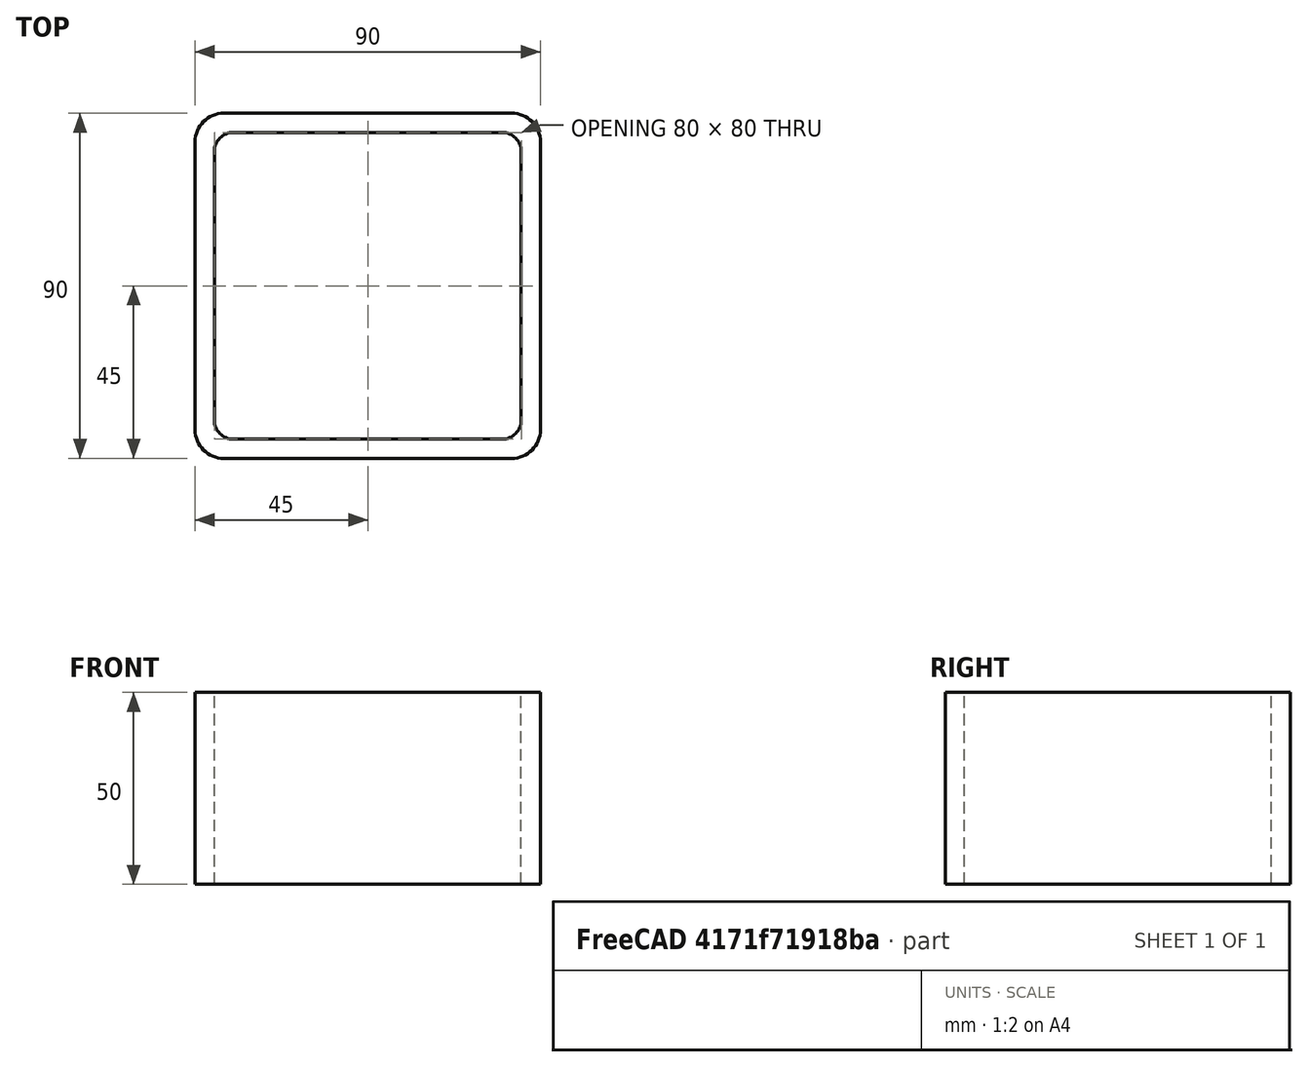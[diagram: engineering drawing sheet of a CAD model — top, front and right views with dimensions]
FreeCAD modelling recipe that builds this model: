
FCSTD DOCUMENT  (FreeCAD 0.15R4671 (Git))
Label: Square hollow section 90x90x5 EN10219 S235JRH
License: All rights reserved
LicenseURL: http://en.wikipedia.org/wiki/All_rights_reserved
objects: Sketcher::SketchObject×1, Part::Extrusion×1
note: 2 computed .brp shape members not serialized (recipe doc carries the construction recipe); baked Part::Feature solids carry a one-line shape summary decoded from their .brp

FEATURE [Sketcher::SketchObject] Sketch
  sketch-geometry (16):
    g0: LineSegment StartX=-35 StartY=40 StartZ=0 EndX=35 EndY=40 EndZ=0
    g1: LineSegment StartX=40 StartY=35 StartZ=0 EndX=40 EndY=-35 EndZ=0
    g2: LineSegment StartX=35 StartY=-40 StartZ=0 EndX=-35 EndY=-40 EndZ=0
    g3: LineSegment StartX=-40 StartY=-35 StartZ=0 EndX=-40 EndY=35 EndZ=0
    g4: LineSegment StartX=-37.5 StartY=45 StartZ=0 EndX=37.5 EndY=45 EndZ=0
    g5: LineSegment StartX=45 StartY=37.5 StartZ=0 EndX=45 EndY=-37.5 EndZ=0
    g6: LineSegment StartX=37.5 StartY=-45 StartZ=0 EndX=-37.5 EndY=-45 EndZ=0
    g7: LineSegment StartX=-45 StartY=-37.5 StartZ=0 EndX=-45 EndY=37.5 EndZ=0
    g8: ArcOfCircle CenterX=-35 CenterY=35 CenterZ=0 NormalX=0 NormalY=0 NormalZ=1 Radius=5 StartAngle=1.5708 EndAngle=3.14159
    g9: ArcOfCircle CenterX=35 CenterY=35 CenterZ=0 NormalX=0 NormalY=0 NormalZ=1 Radius=5 StartAngle=0 EndAngle=1.5708
    g10: ArcOfCircle CenterX=35 CenterY=-35 CenterZ=0 NormalX=0 NormalY=0 NormalZ=1 Radius=5 StartAngle=4.71239 EndAngle=6.28319
    g11: ArcOfCircle CenterX=-35 CenterY=-35 CenterZ=0 NormalX=0 NormalY=0 NormalZ=1 Radius=5 StartAngle=3.14159 EndAngle=4.71239
    g12: ArcOfCircle CenterX=37.5 CenterY=37.5 CenterZ=0 NormalX=0 NormalY=0 NormalZ=1 Radius=7.5 StartAngle=0 EndAngle=1.5708
    g13: ArcOfCircle CenterX=37.5 CenterY=-37.5 CenterZ=0 NormalX=0 NormalY=0 NormalZ=1 Radius=7.5 StartAngle=4.71239 EndAngle=6.28319
    g14: ArcOfCircle CenterX=-37.5 CenterY=-37.5 CenterZ=0 NormalX=0 NormalY=0 NormalZ=1 Radius=7.5 StartAngle=3.14159 EndAngle=4.71239
    g15: ArcOfCircle CenterX=-37.5 CenterY=37.5 CenterZ=0 NormalX=0 NormalY=0 NormalZ=1 Radius=7.5 StartAngle=1.5708 EndAngle=3.14159
  constraints (36):
    c: Horizontal(g2)
    c: Vertical(g3)
    c: Horizontal(g6)
    c: Vertical(g7)
    c: Tangent(g3,g8) = 1.5708
    c: Tangent(g0,g8) = 1.5708
    c: Tangent(g0,g9) = 1.5708
    c: Tangent(g1,g9) = 1.5708
    c: Tangent(g1,g10) = 1.5708
    c: Tangent(g2,g10) = 1.5708
    c: Tangent(g2,g11) = 1.5708
    c: Tangent(g3,g11) = 1.5708
    c: Tangent(g4,g12) = 1.5708
    c: Tangent(g5,g12) = 1.5708
    c: Tangent(g5,g13) = 1.5708
    c: Tangent(g6,g13) = 1.5708
    c: Tangent(g6,g14) = 1.5708
    c: Tangent(g7,g14) = 1.5708
    c: Tangent(g7,g15) = 1.5708
    c: Tangent(g4,g15) = 1.5708
    c: Equal(g9,g8)
    c: Equal(g9,g11)
    c: Equal(g9,g10)
    c: Equal(g12,g15)
    c: Equal(g12,g14)
    c: Equal(g12,g13)
    c: Symmetric(g4,g6,g-1)
    c: Symmetric(g7,g5,g-2)
    c: DistanceY(g4,g6) = -90
    c: DistanceX(g7,g5) = 90
    c: Symmetric(g3,g1,g-2)
    c: Symmetric(g0,g2,g-1)
    c: DistanceY(g0,g4) = 5
    c: DistanceX(g5,g1) = -5
    c: Radius(g9) = 5
    c: Radius(g12) = 7.5
FEATURE [Part::Extrusion] Extrude  label="Square hollow section 90x90x5 EN10219 S235JRH"
  Base = -> Sketch
  Dir = (0,0,50)
  Solid = true
